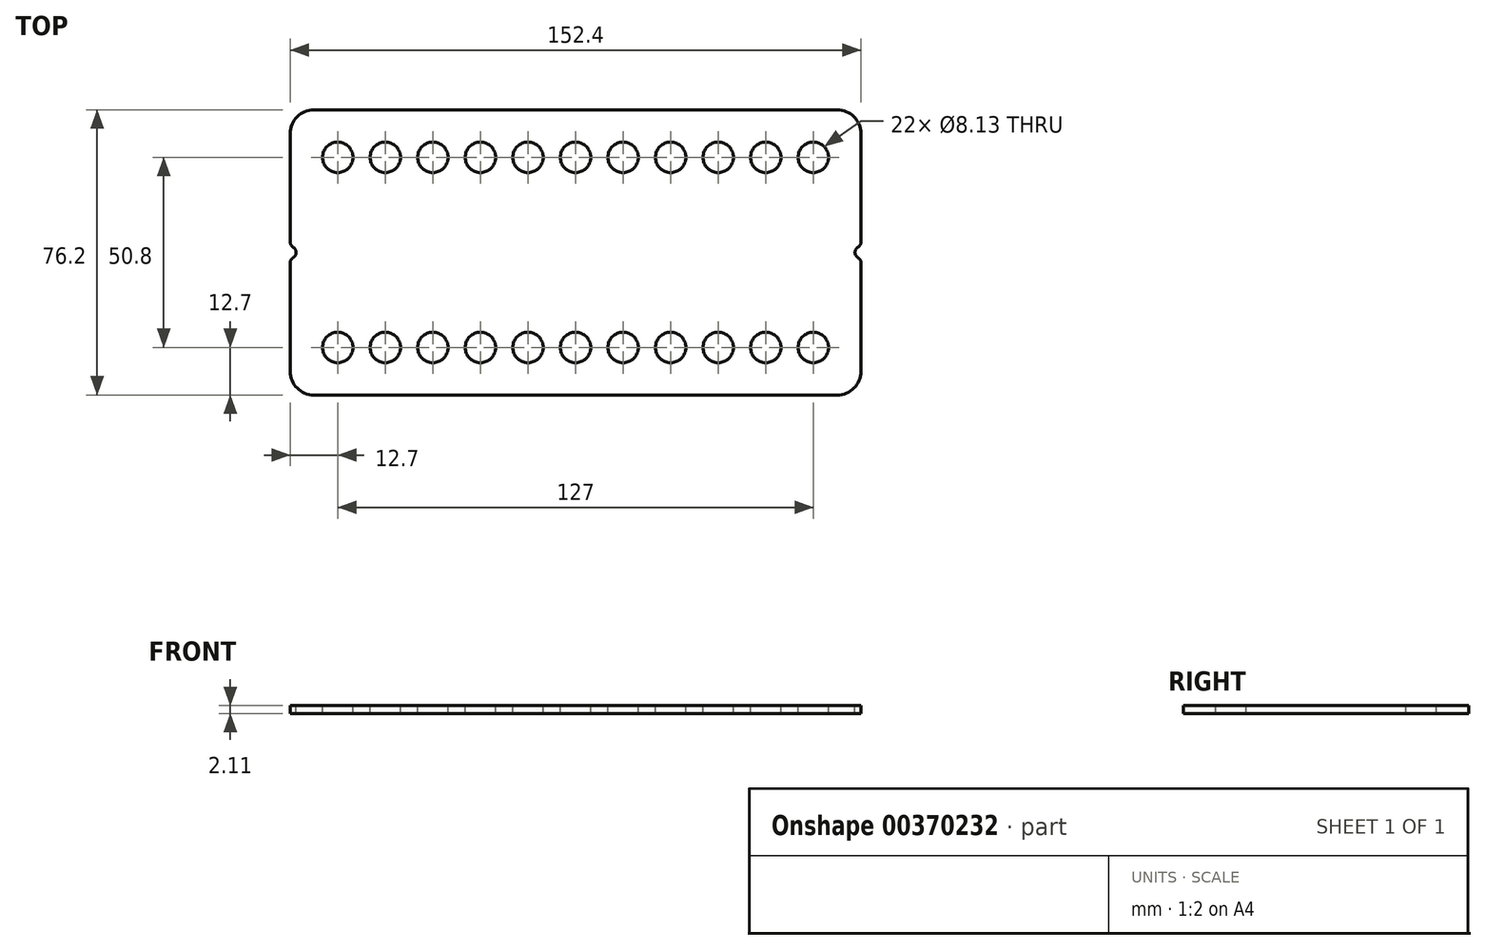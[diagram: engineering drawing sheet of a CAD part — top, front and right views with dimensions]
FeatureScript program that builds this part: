
annotation { "Feature Type Name" : "Feature", "Feature Type Description" : "" }
export const myFeature = defineFeature(function(context is Context, id is Id, definition is map)
    precondition{}
    {
        {
            var Q0;
            Q0=qCreatedBy(makeId("Top.planeOp"),FACE);
            var sketch = newSketch(context, id + "F0", { "sketchPlane" : qUnion([Q0])});
            skLineSegment(sketch, "E0.bottom", {"start": v(-69.85, 38.1) * mm, "end": v(69.85, 38.1) * mm});
            skLineSegment(sketch, "E0.top", {"start": v(-69.85, -38.1) * mm, "end": v(69.85, -38.1) * mm});
            skLineSegment(sketch, "E0.left", {"start": v(-76.2, 31.75) * mm, "end": v(-76.2, 2.75) * mm});
            skLineSegment(sketch, "E0.right", {"start": v(76.2, 31.75) * mm, "end": v(76.2, 2.75) * mm});
            skLineSegment(sketch, "E1", {"start": v(-76.2, 38.1) * mm, "end": v(76.2, -38.1) * mm, "construction": true});
            skLineSegment(sketch, "E2", {"start": v(-76.2, 0) * mm, "end": v(76.2, 0) * mm, "construction": true});
            skCircle(sketch, "E3", {"center": v(0, 25.4) * mm, "radius": 4.06 * mm});
            skCircle(sketch, "E4.1.0.0", {"center": v(12.7, 25.4) * mm, "radius": 4.06 * mm});
            skCircle(sketch, "E4.2.0.0", {"center": v(25.4, 25.4) * mm, "radius": 4.06 * mm});
            skLineSegment(sketch, "E4.direction1", {"start": v(0, 25.4) * mm, "end": v(12.7, 25.4) * mm, "construction": true});
            skCircle(sketch, "E5.1.0.0", {"center": v(-12.7, 25.4) * mm, "radius": 4.06 * mm});
            skCircle(sketch, "E5.2.0.0", {"center": v(-25.4, 25.4) * mm, "radius": 4.06 * mm});
            skLineSegment(sketch, "E5.direction1", {"start": v(0, 25.4) * mm, "end": v(-12.7, 25.4) * mm, "construction": true});
            skCircle(sketch, "E6.MirrorC", {"center": v(-25.4, -25.4) * mm, "radius": 4.06 * mm});
            skCircle(sketch, "E7.MirrorC", {"center": v(-12.7, -25.4) * mm, "radius": 4.06 * mm});
            skCircle(sketch, "E8.MirrorC", {"center": v(0, -25.4) * mm, "radius": 4.06 * mm});
            skCircle(sketch, "E9.MirrorC", {"center": v(12.7, -25.4) * mm, "radius": 4.06 * mm});
            skCircle(sketch, "E10.MirrorC", {"center": v(25.4, -25.4) * mm, "radius": 4.06 * mm});
            skPoint(sketch, "E11.visualSharp", {"position": v(-76.2, 38.1) * mm});
            skArc(sketch, "E11.filletArc", {"start": v(-69.85, 38.1) * mm, "mid": v(-74.34, 36.24) * mm, "end": v(-76.2, 31.75) * mm});
            skPoint(sketch, "E12.visualSharp", {"position": v(-76.2, -38.1) * mm});
            skArc(sketch, "E12.filletArc", {"start": v(-76.2, -31.75) * mm, "mid": v(-74.34, -36.24) * mm, "end": v(-69.85, -38.1) * mm});
            skPoint(sketch, "E13.visualSharp", {"position": v(76.2, -38.1) * mm});
            skArc(sketch, "E13.filletArc", {"start": v(69.85, -38.1) * mm, "mid": v(74.34, -36.24) * mm, "end": v(76.2, -31.75) * mm});
            skPoint(sketch, "E14.visualSharp", {"position": v(76.2, 38.1) * mm});
            skArc(sketch, "E14.filletArc", {"start": v(76.2, 31.75) * mm, "mid": v(74.34, 36.24) * mm, "end": v(69.85, 38.1) * mm});
            skCircle(sketch, "E15.0.3.0", {"center": v(-38.1, 25.4) * mm, "radius": 4.06 * mm});
            skCircle(sketch, "E16.0.3.0", {"center": v(38.1, 25.4) * mm, "radius": 4.06 * mm});
            skCircle(sketch, "E17.MirrorC", {"center": v(-38.1, -25.4) * mm, "radius": 4.06 * mm});
            skCircle(sketch, "E18.MirrorC", {"center": v(38.1, -25.4) * mm, "radius": 4.06 * mm});
            skCircle(sketch, "E19.0.4.0", {"center": v(50.8, 25.4) * mm, "radius": 4.06 * mm});
            skCircle(sketch, "E20.0.4.0", {"center": v(-50.8, 25.4) * mm, "radius": 4.06 * mm});
            skCircle(sketch, "E21.MirrorC", {"center": v(50.8, -25.4) * mm, "radius": 4.06 * mm});
            skCircle(sketch, "E22.MirrorC", {"center": v(-50.8, -25.4) * mm, "radius": 4.06 * mm});
            skArc(sketch, "E23", {"start": v(-75.4, -1.37) * mm, "mid": v(-74.61, 0) * mm, "end": v(-75.4, 1.37) * mm});
            skArc(sketch, "E24", {"start": v(75.4, 1.37) * mm, "mid": v(74.61, 0) * mm, "end": v(75.4, -1.37) * mm});
            skLineSegment(sketch, "E25.trimOffspring", {"start": v(-76.2, -2.75) * mm, "end": v(-76.2, -31.75) * mm});
            skLineSegment(sketch, "E26.trimOffspring", {"start": v(76.2, -2.75) * mm, "end": v(76.2, -31.75) * mm});
            skPoint(sketch, "E27.visualSharp", {"position": v(76.2, 1.59) * mm});
            skArc(sketch, "E27.filletArc", {"start": v(75.4, 1.37) * mm, "mid": v(75.99, 1.96) * mm, "end": v(76.2, 2.75) * mm});
            skPoint(sketch, "E28.visualSharp", {"position": v(76.2, -1.59) * mm});
            skArc(sketch, "E28.filletArc", {"start": v(76.2, -2.75) * mm, "mid": v(75.99, -1.96) * mm, "end": v(75.4, -1.37) * mm});
            skPoint(sketch, "E29.visualSharp", {"position": v(-76.2, 1.59) * mm});
            skArc(sketch, "E29.filletArc", {"start": v(-76.2, 2.75) * mm, "mid": v(-75.99, 1.96) * mm, "end": v(-75.4, 1.37) * mm});
            skPoint(sketch, "E30.visualSharp", {"position": v(-76.2, -1.59) * mm});
            skArc(sketch, "E30.filletArc", {"start": v(-75.4, -1.37) * mm, "mid": v(-75.99, -1.96) * mm, "end": v(-76.2, -2.75) * mm});
            skLineSegment(sketch, "E31", {"start": v(0, -42.5) * mm, "end": v(0, 57.76) * mm, "construction": true});
            skCircle(sketch, "E32.0.5.0", {"center": v(-63.5, 25.4) * mm, "radius": 4.06 * mm});
            skCircle(sketch, "E33.0.5.0", {"center": v(63.5, 25.4) * mm, "radius": 4.06 * mm});
            skCircle(sketch, "E34.MirrorC", {"center": v(63.5, -25.4) * mm, "radius": 4.06 * mm});
            skCircle(sketch, "E35.MirrorC", {"center": v(-63.5, -25.4) * mm, "radius": 4.06 * mm});
            skSolve(sketch);
        }
        {
            var Q0;
            Q0=makeQuery(id+"F0.imprint","IMPRINT",FACE,{"disambiguationData":[TD([[makeQuery(id+"F0.imprint","IMPRINT",EDGE,{"derivedFrom":sQuery(id+"F0.wireOp",EDGE,"E0.bottom")}),-1.0]])]});
            extrude(context, id + "F1", {"entities" : qUnion([Q0]), "oppositeDirection" : true, "depth" : 2.1 * mm});
        }
    });
